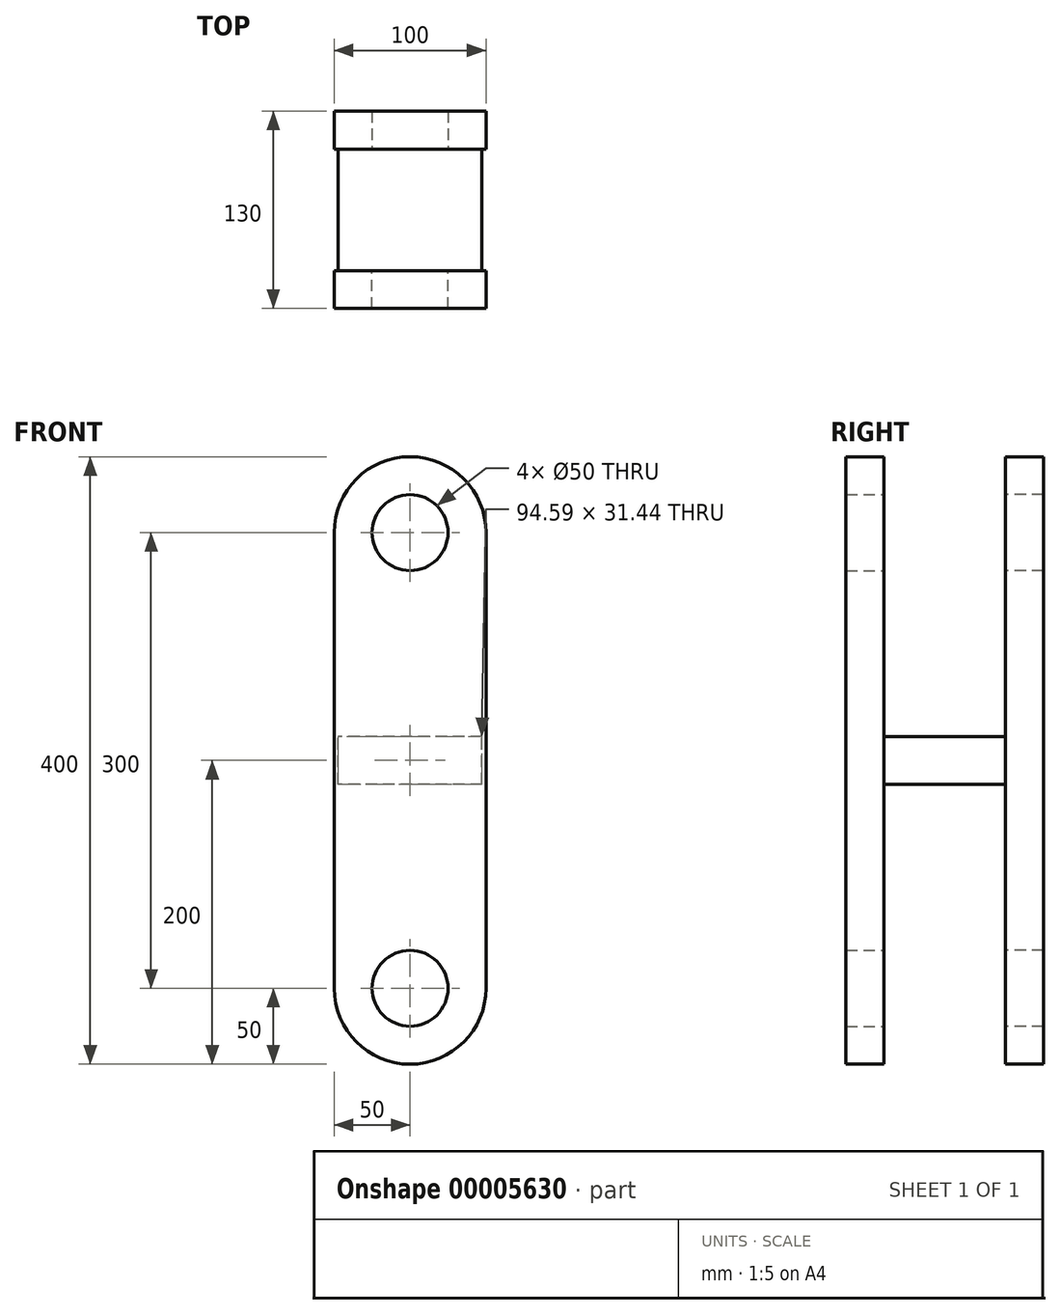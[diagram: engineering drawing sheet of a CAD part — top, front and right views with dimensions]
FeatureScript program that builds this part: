
annotation { "Feature Type Name" : "Feature", "Feature Type Description" : "" }
export const myFeature = defineFeature(function(context is Context, id is Id, definition is map)
    precondition{}
    {
        {
            var Q0;
            Q0=qCreatedBy(makeId("Front.planeOp"),FACE);
            cPlane(context, id + "F0", {"entities" : qUnion([Q0]), "cplaneType" : CPlaneType.OFFSET, "offset" : 40 * mm, "width" : 150 * mm, "height" : 150 * mm});
        }
        {
            var Q0;
            Q0=qCreatedBy(id+"F0.planeOp",FACE);
            var sketch = newSketch(context, id + "F1", { "sketchPlane" : qUnion([Q0])});
            skLineSegment(sketch, "E0.rect.bottom", {"start": v(50, 150) * mm, "end": v(-50, 150) * mm});
            skLineSegment(sketch, "E0.rect.top", {"start": v(50, -150) * mm, "end": v(-50, -150) * mm});
            skLineSegment(sketch, "E0.rect.left", {"start": v(50, 150) * mm, "end": v(50, -150) * mm});
            skLineSegment(sketch, "E0.rect.right", {"start": v(-50, 150) * mm, "end": v(-50, -150) * mm});
            skPoint(sketch, "E0.rect.middle", {"position": v(0, 0) * mm});
            skArc(sketch, "E1", {"start": v(50, 150) * mm, "mid": v(0, 200) * mm, "end": v(-50, 150) * mm});
            skCircle(sketch, "E2", {"center": v(0, 150) * mm, "radius": 25 * mm});
            skArc(sketch, "E3", {"start": v(-50, -150) * mm, "mid": v(0, -200) * mm, "end": v(50, -150) * mm});
            skCircle(sketch, "E4", {"center": v(0, -150) * mm, "radius": 25 * mm});
            skSolve(sketch);
        }
        {
            var Q0;
            {var subQ0=sQuery(id+"F1.wireOp",EDGE,"E1");Q0=makeQuery(id+"F1.imprint","IMPRINT",FACE,{"disambiguationData":[TD([[makeQuery(id+"F1.imprint","IMPRINT",EDGE,{"derivedFrom":subQ0}),1.0]])]});}
            var Q1;
            Q1=makeQuery(id+"F1.imprint","IMPRINT",FACE,{"disambiguationData":[TD([[makeQuery(id+"F1.imprint","IMPRINT",EDGE,{"derivedFrom":sQuery(id+"F1.wireOp",EDGE,"E0.rect.top")}),-1.0]])]});
            var Q2;
            {var subQ4=sQuery(id+"F1.wireOp",EDGE,"E3");Q2=makeQuery(id+"F1.imprint","IMPRINT",FACE,{"disambiguationData":[TD([[makeQuery(id+"F1.imprint","IMPRINT",EDGE,{"derivedFrom":subQ4}),1.0]])]});}
            extrude(context, id + "F2", {"entities" : qUnion([Q0, Q1, Q2]), "depth" : 25 * mm});
        }
        {
            var Q0;
            Q0=makeQuery(id+"F2.opExtrude","SWEPT_BODY",BODY,{"disambiguationData":[OSD([sQuery(id+"F1.wireOp",EDGE,"E0.rect.top"),sQuery(id+"F1.wireOp",EDGE,"E0.rect.left"),sQuery(id+"F1.wireOp",EDGE,"E0.rect.right"),sQuery(id+"F1.wireOp",EDGE,"E1"),sQuery(id+"F1.wireOp",EDGE,"E2")])]});
            var Q1;
            Q1=qCreatedBy(makeId("Front.planeOp"),FACE);
            mirror(context, id + "F3", {"entities" : qUnion([Q0]), "mirrorPlane" : qUnion([Q1])});
        }
        {
            var Q0;
            Q0=qCreatedBy(makeId("Right.planeOp"),FACE);
            var sketch = newSketch(context, id + "F4", { "sketchPlane" : qUnion([Q0])});
            skLineSegment(sketch, "E5.rect.bottom", {"start": v(61.43, 15.72) * mm, "end": v(-61.43, 15.72) * mm});
            skLineSegment(sketch, "E5.rect.top", {"start": v(61.43, -15.72) * mm, "end": v(-61.43, -15.72) * mm});
            skLineSegment(sketch, "E5.rect.left", {"start": v(61.43, 15.72) * mm, "end": v(61.43, -15.72) * mm});
            skLineSegment(sketch, "E5.rect.right", {"start": v(-61.43, 15.72) * mm, "end": v(-61.43, -15.72) * mm});
            skPoint(sketch, "E5.rect.middle", {"position": v(0, 0) * mm});
            skSolve(sketch);
        }
        {
            var Q0;
            Q0=makeQuery(id+"F4.imprint","IMPRINT",FACE,{"disambiguationData":[TD([[makeQuery(id+"F4.imprint","IMPRINT",EDGE,{"derivedFrom":sQuery(id+"F4.wireOp",EDGE,"E5.rect.bottom")}),1.0]])]});
            var Q1;
            Q1=makeQuery(id+"F2.opExtrude","SWEPT_FACE",FACE,{"disambiguationData":[OSD([sQuery(id+"F1.wireOp",EDGE,"E0.rect.left")])]});
            extrude(context, id + "F5", {"entities" : qUnion([Q0]), "operationType" : NewBodyOperationType.ADD, "endBound" : BoundingType.SYMMETRIC, "oppositeDirection" : true, "endBoundEntity" : qUnion([Q1]), "depth" : 94.6 * mm});
        }
    });
